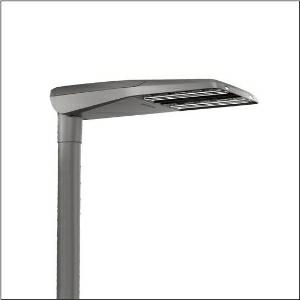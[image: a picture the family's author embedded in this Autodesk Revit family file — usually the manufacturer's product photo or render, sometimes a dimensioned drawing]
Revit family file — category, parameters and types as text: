
# Revit family: streetlight_sl_11_iq_midi___st1_0st0_5_5xc3j51f08me_a600
name_source: partatom
category: Lighting Fixtures
units: mm (PartAtom-declared; Revit-internal decimal feet)

## family parameters
Cut with Voids When Loaded = No
Host = Face
Light Source = No
Part Type = Normal
Room Calculation Point = No
Round Connector Dimension = Use Diameter
Shared = No

## types (1)
- --- (1 x LED, 17650 lm, 124.7 W, 3000K)
    Apparent Load = 125 VA
    CIE Flux Codes = 35 68 96 100 100
    Color Rendering = 70
    Color Temperature = 3000K
    Default Elevation = 1800 mm
    Description = Streetlight SL 11 iQ midi, mast luminaire, primary light control with 3 zone facetted reflector, of plastic, silver coated, highly specular, primary optical cover: cover, of PMMA, transparent, light distribution: ST1.0ST0.5, light emission: direct distribution, primary light characteristic: asymmetric, installation type: post-top, side-entry, lamps: LED, High Power LED, rated values: 17.650lm | 124,7W | 141,5lm/W (begin service life); end service life: 17.650lm | 132,2W; at 50% lumin. flux: 8.825lm | 57,2W | 154,3lm/W, colour temperature: 3000K, colour rendering: CRI > 70, light colour: 730, light setting 1 begin service life: 100% | 17.650lm | 124,7W | 141,5lm/W | 3.000K, light setting 1 end service life: 132,2W, further light settings possible, control: Street-Remote, Auto-Match, Temp-Guard, Lumen-Switch, Night-Set, Smart-Wire, Light-Fading, Desk-Remote (wireless, voltage-free reading and setting of iQ features in the workshop via application-optimized NFC function/RFID function), optimised constant luminous flux control (CLO 2.0), with cable H07RN-F 5x 1.5mm², mains connection: 230..240V, AC, 50/60Hz, connection cable pre-assembled, cable length: 12,5m, luminaire housing, of diecast aluminium, powder-coated, Siteco® metallic grey (DB 702S), please order mast flange separately, inclination adjustable without tools: 0°, 5°, 10°, 15° (post-top) | 0°, -5°, -10°, -15° (side-entry), sealing non-destructively replaceable, multi-level sealing system, length: 780mm, width: 376mm, height: 118mm, mast flange for spigot size: 42mm (side-entry): 5XC10008XM4, 60/48mm (side-entry/post-top): 5XC10108XM2, 76/60mm (side-entry/post-top): 5XC10108XM1, equipment: Power, protection rating (complete): IP66, insulation class (complete): insulation class II (safety insulation), certification: CE, ENEC, ENEC+, VDE, impact resistance: IK10, permissible operating ambient temperature for outdoor applications: -25..+50°C, standard-compliant lighting for roads and squares, Environmental Product Declaration (EPD) tested and certified by an independent institute, packaging unit: 1 piece

Light Distribution: ST1.0ST0.5
    Height = 118 mm
    Lamp = 1 x LED
    Lamp Light Flux = 17650 lm
    Lamp Power = 124.7 W
    Lamp count = 1
    Length = 780 mm
    Luminous efficacy = 142 lm/W
    Manufacturer = Siteco
    ModVariant = No
    Model = 5XC3J51F08ME
    Number of Poles = 1
    OnlyDefault = Yes
    Power Factor = 1
    Product Name = Streetlight SL 11 iQ midi | ST1.0ST0.5
    Product group = mast luminaire | pylon top
    ProductGroupID = 6100
    Protection Class = Protection class II
    Protection Degree = IP 66
    RLX_Detail_Level = 1
    RLX_Emergency_Light_Flux = 0 lm
    RLX_Emergency_Type = 0
    RLX_Emergency_Type_DB = No
    RlxData = <blob elided: 70861 chars, md5=de2fd068>
    Socket = socket
    Standby Power = 0 W
    System Light Flux = 17650 lm
    System Power = 125 W
    Type Comments = factory setting: luminous flux: 100 % | dim-lin: 254 | 557 mA
    Type Image = l_1005960.jpg
    URL = http://relux.com
    VarID = @adj_061175
    Voltage = 0 V
    Weight = 0.00 kg
    Width = 376 mm

## geometry (parser evidence)
native form markers: Blend x4, Sweep x9
no freeform markers — native parametric forms only
